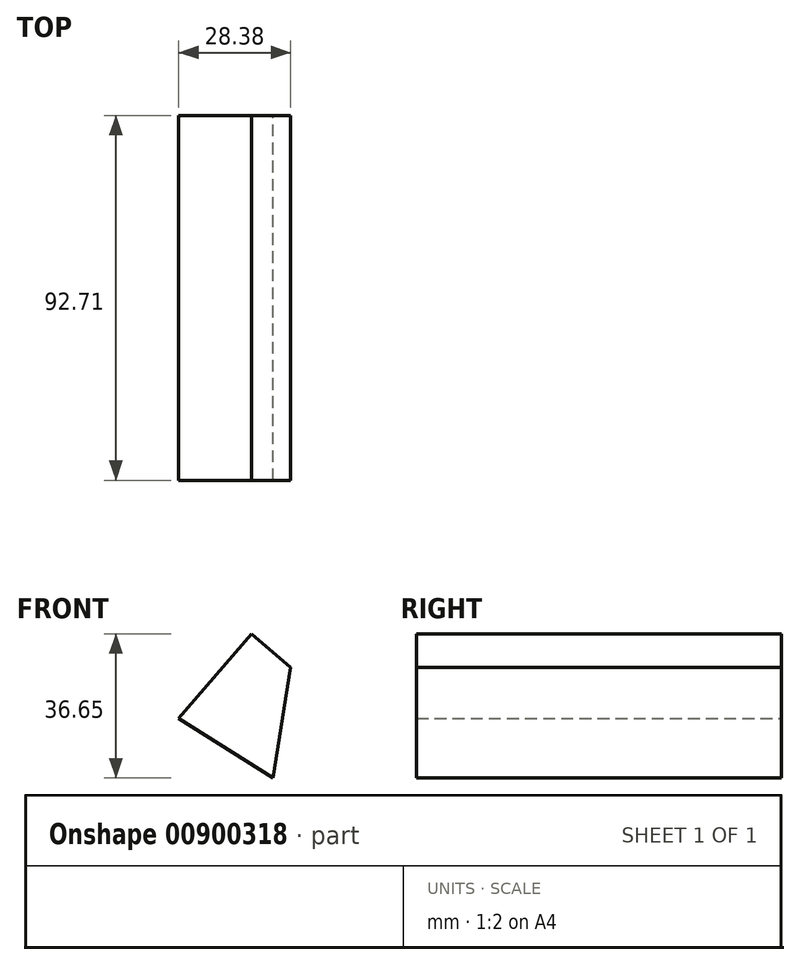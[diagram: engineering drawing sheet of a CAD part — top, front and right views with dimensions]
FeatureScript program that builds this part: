
annotation { "Feature Type Name" : "Feature", "Feature Type Description" : "" }
export const myFeature = defineFeature(function(context is Context, id is Id, definition is map)
    precondition{}
    {
        {
            var Q0;
            Q0=qCreatedBy(makeId("Front.planeOp"),FACE);
            var sketch = newSketch(context, id + "F0", { "sketchPlane" : qUnion([Q0])});
            skLineSegment(sketch, "E0", {"start": v(0, 0) * mm, "end": v(18.48, 21.53) * mm});
            skLineSegment(sketch, "E1", {"start": v(18.48, 21.53) * mm, "end": v(28.38, 13.03) * mm});
            skLineSegment(sketch, "E2", {"start": v(28.38, 13.03) * mm, "end": v(23.97, -15.12) * mm});
            skLineSegment(sketch, "E3", {"start": v(23.97, -15.12) * mm, "end": v(0, 0) * mm});
            skSolve(sketch);
        }
        {
            var Q0;
            Q0 = qSketchRegion(id + "F0", true);
            extrude(context, id + "F1", {"entities" : qUnion([Q0]), "depth" : 25.4 * mm, "offsetDistance" : 25.4 * mm, "hasSecondDirection" : true, "secondDirectionOppositeDirection" : true, "secondDirectionDepth" : 41.9 * mm});
        }
        {
            var Q0;
            Q0=makeQuery(id+"F1.opExtrude","CAP_FACE",FACE,{"disambiguationData":[OSD([sQuery(id+"F0.wireOp",EDGE,"E0"),sQuery(id+"F0.wireOp",EDGE,"E1"),sQuery(id+"F0.wireOp",EDGE,"E2"),sQuery(id+"F0.wireOp",EDGE,"E3")])],"isStart":false});
            var sketch = newSketch(context, id + "F2", { "sketchPlane" : qUnion([Q0])});
            skSolve(sketch);
        }
        {
            var Q0;
            Q0 = qSketchRegion(id + "F2", true);
            var Q1;
            Q1=makeQuery(id+"F1.opExtrude","CAP_FACE",FACE,{"disambiguationData":[OSD([sQuery(id+"F0.wireOp",EDGE,"E0"),sQuery(id+"F0.wireOp",EDGE,"E1"),sQuery(id+"F0.wireOp",EDGE,"E2"),sQuery(id+"F0.wireOp",EDGE,"E3")])],"isStart":false});
            extrude(context, id + "F3", {"entities" : qUnion([Q0, Q1]), "operationType" : NewBodyOperationType.ADD, "depth" : 25.4 * mm, "offsetDistance" : 25.4 * mm});
        }
    });
